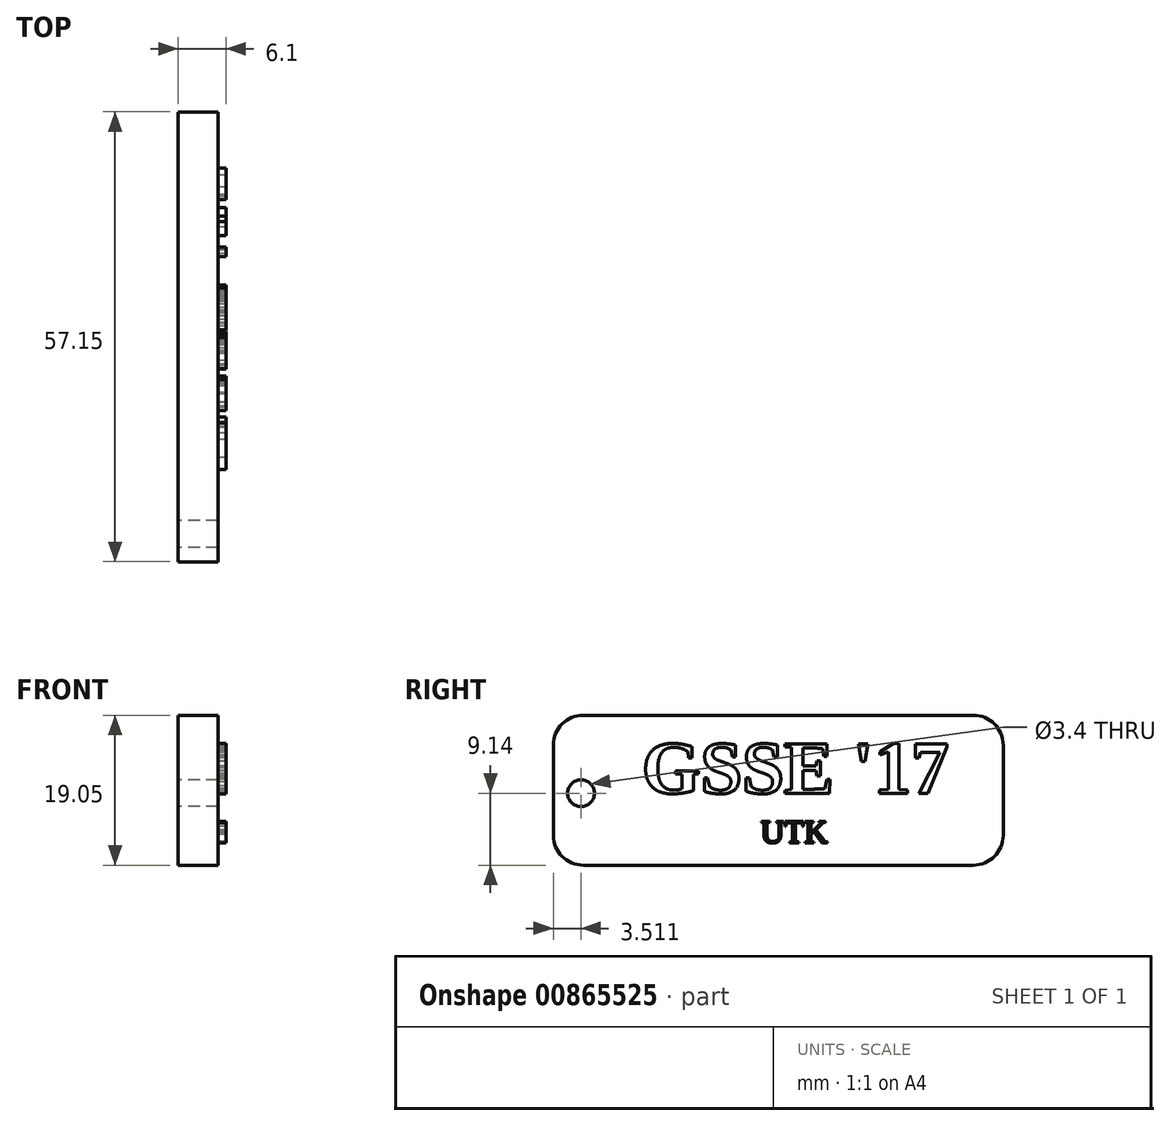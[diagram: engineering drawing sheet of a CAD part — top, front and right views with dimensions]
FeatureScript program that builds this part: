
annotation { "Feature Type Name" : "Feature", "Feature Type Description" : "" }
export const myFeature = defineFeature(function(context is Context, id is Id, definition is map)
    precondition{}
    {
        {
            var Q0;
            Q0=qCreatedBy(makeId("Right.planeOp"),FACE);
            var sketch = newSketch(context, id + "F0", { "sketchPlane" : qUnion([Q0])});
            skLineSegment(sketch, "E0.bottom", {"start": v(-24.1, 9.91) * mm, "end": v(25.44, 9.91) * mm});
            skLineSegment(sketch, "E0.top", {"start": v(-24.1, -9.14) * mm, "end": v(25.44, -9.14) * mm});
            skLineSegment(sketch, "E0.left", {"start": v(-27.9, 6.1) * mm, "end": v(-27.9, -5.33) * mm});
            skLineSegment(sketch, "E0.right", {"start": v(29.25, 6.1) * mm, "end": v(29.25, -5.33) * mm});
            skPoint(sketch, "E1.visualSharp", {"position": v(-27.9, 9.91) * mm});
            skArc(sketch, "E1.filletArc", {"start": v(-24.1, 9.91) * mm, "mid": v(-26.79, 8.8) * mm, "end": v(-27.9, 6.1) * mm});
            skPoint(sketch, "E2.visualSharp", {"position": v(29.25, 9.91) * mm});
            skArc(sketch, "E2.filletArc", {"start": v(29.25, 6.1) * mm, "mid": v(28.13, 8.8) * mm, "end": v(25.44, 9.91) * mm});
            skPoint(sketch, "E3.visualSharp", {"position": v(29.25, -9.14) * mm});
            skArc(sketch, "E3.filletArc", {"start": v(25.44, -9.14) * mm, "mid": v(28.13, -8.02) * mm, "end": v(29.25, -5.33) * mm});
            skPoint(sketch, "E4.visualSharp", {"position": v(-27.9, -9.14) * mm});
            skArc(sketch, "E4.filletArc", {"start": v(-27.9, -5.33) * mm, "mid": v(-26.79, -8.02) * mm, "end": v(-24.1, -9.14) * mm});
            skLineSegment(sketch, "E5", {"start": v(-40.67, 0) * mm, "end": v(41.33, 0) * mm, "construction": true});
            skCircle(sketch, "E6", {"center": v(-24.39, 0) * mm, "radius": 1.7 * mm});
            skSolve(sketch);
        }
        {
            var Q0;
            Q0 = qSketchRegion(id + "F0", true);
            extrude(context, id + "F1", {"entities" : qUnion([Q0]), "depth" : 5.08 * mm, "offsetDistance" : 25.4 * mm});
        }
        {
            var Q0;
            Q0=qCreatedBy(makeId("Right.planeOp"),FACE);
            var sketch = newSketch(context, id + "F2", { "sketchPlane" : qUnion([Q0])});
            skText(sketch, "E7", { "text": "GSSE \'17", "fontName": "Tinos-Bold.ttf"});
            skText(sketch, "E8", { "text": "UTK", "fontName": "Tinos-Regular.ttf"});
            const initialGuessF2  = {"E7": [-0.01665, 0, 1, 0, 0.00687], "E8": [-0.00157, -0.0063, 1, 0, 0.00298]};
            skSetInitialGuess(sketch, initialGuessF2);
            skSolve(sketch);
        }
        {
            var Q0;
            Q0 = qSketchRegion(id + "F2", true);
            extrude(context, id + "F3", {"entities" : qUnion([Q0]), "operationType" : NewBodyOperationType.ADD, "depth" : 6.1 * mm, "offsetDistance" : 25.4 * mm});
        }
    });
